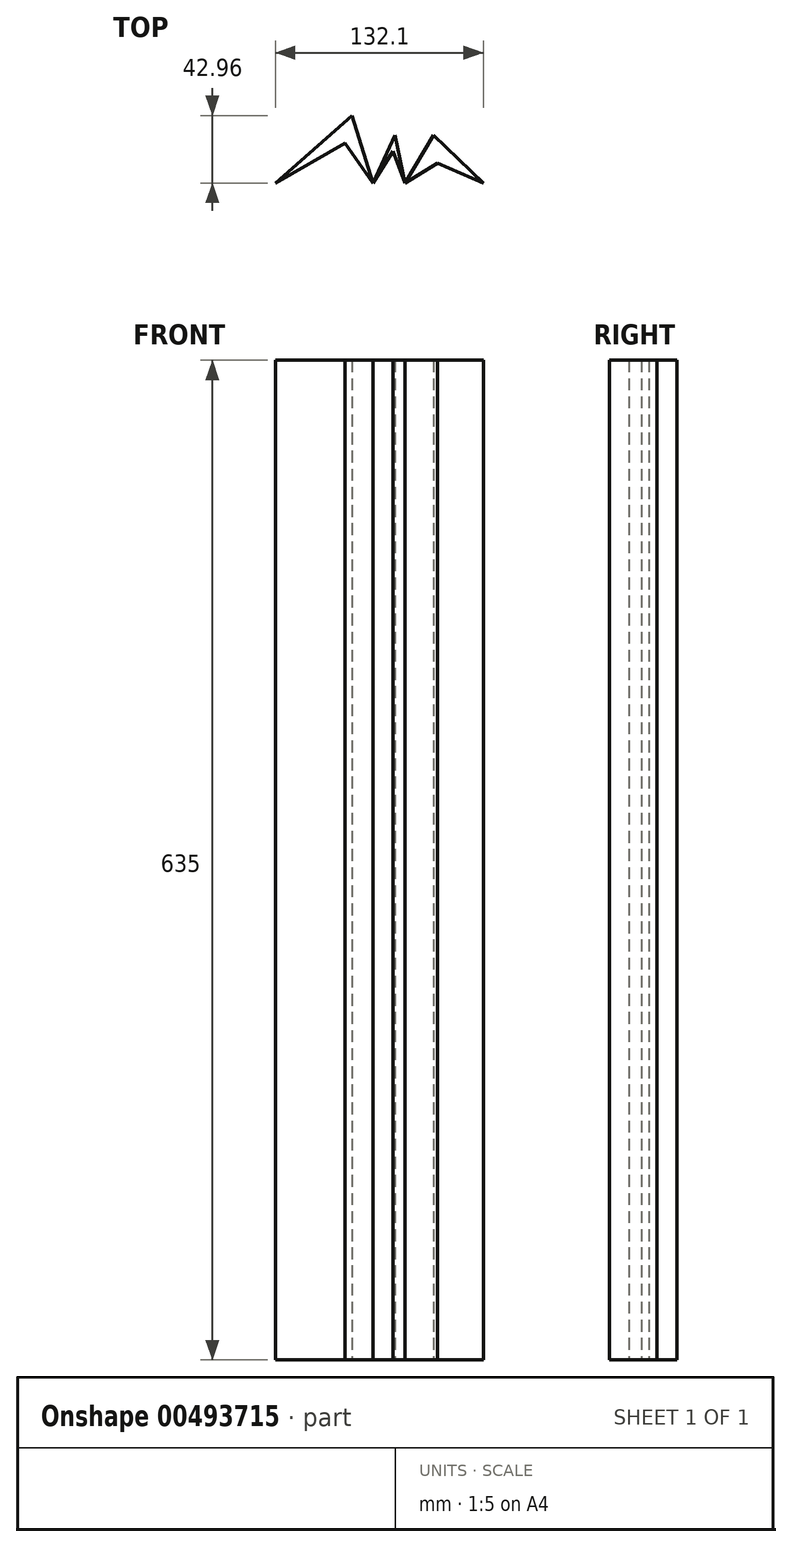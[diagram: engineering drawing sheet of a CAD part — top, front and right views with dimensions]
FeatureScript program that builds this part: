
annotation { "Feature Type Name" : "Feature", "Feature Type Description" : "" }
export const myFeature = defineFeature(function(context is Context, id is Id, definition is map)
    precondition{}
    {
        {
            var Q0;
            Q0=qCreatedBy(makeId("Top.planeOp"),FACE);
            var sketch = newSketch(context, id + "F0", { "sketchPlane" : qUnion([Q0])});
            skLineSegment(sketch, "E0", {"start": v(-58.53, 0) * mm, "end": v(-9.93, 42.96) * mm});
            skLineSegment(sketch, "E1", {"start": v(-9.93, 42.96) * mm, "end": v(3.5, 0) * mm});
            skLineSegment(sketch, "E2", {"start": v(3.5, 0) * mm, "end": v(17.45, 30.34) * mm});
            skLineSegment(sketch, "E3", {"start": v(17.45, 30.34) * mm, "end": v(23.9, 0) * mm});
            skLineSegment(sketch, "E4", {"start": v(23.9, 0) * mm, "end": v(41.88, 30.34) * mm});
            skLineSegment(sketch, "E5", {"start": v(41.88, 30.34) * mm, "end": v(73.57, 0) * mm});
            skLineSegment(sketch, "E6", {"start": v(73.57, 0) * mm, "end": v(44.57, 12.62) * mm});
            skLineSegment(sketch, "E7", {"start": v(44.57, 12.62) * mm, "end": v(23.9, 0) * mm});
            skLineSegment(sketch, "E8", {"start": v(23.9, 0) * mm, "end": v(16.08, 20.34) * mm});
            skLineSegment(sketch, "E9", {"start": v(16.08, 20.34) * mm, "end": v(3.5, 0) * mm});
            skLineSegment(sketch, "E10", {"start": v(3.5, 0) * mm, "end": v(-14.31, 25.3) * mm});
            skLineSegment(sketch, "E11", {"start": v(-14.31, 25.3) * mm, "end": v(-58.53, 0) * mm});
            skSolve(sketch);
        }
        {
            var Q0;
            Q0=makeQuery(id+"F0.imprint","IMPRINT",FACE,{"disambiguationData":[TD([[makeQuery(id+"F0.imprint","IMPRINT",EDGE,{"derivedFrom":sQuery(id+"F0.wireOp",EDGE,"E0")}),-1.0]])]});
            var Q1;
            Q1=makeQuery(id+"F0.imprint","IMPRINT",FACE,{"disambiguationData":[TD([[makeQuery(id+"F0.imprint","IMPRINT",EDGE,{"derivedFrom":sQuery(id+"F0.wireOp",EDGE,"E2")}),-1.0]])]});
            var Q2;
            Q2=makeQuery(id+"F0.imprint","IMPRINT",FACE,{"disambiguationData":[TD([[makeQuery(id+"F0.imprint","IMPRINT",EDGE,{"derivedFrom":sQuery(id+"F0.wireOp",EDGE,"E4")}),-1.0]])]});
            extrude(context, id + "F1", {"entities" : qUnion([Q0, Q1, Q2]), "depth" : 635 * mm});
        }
    });
